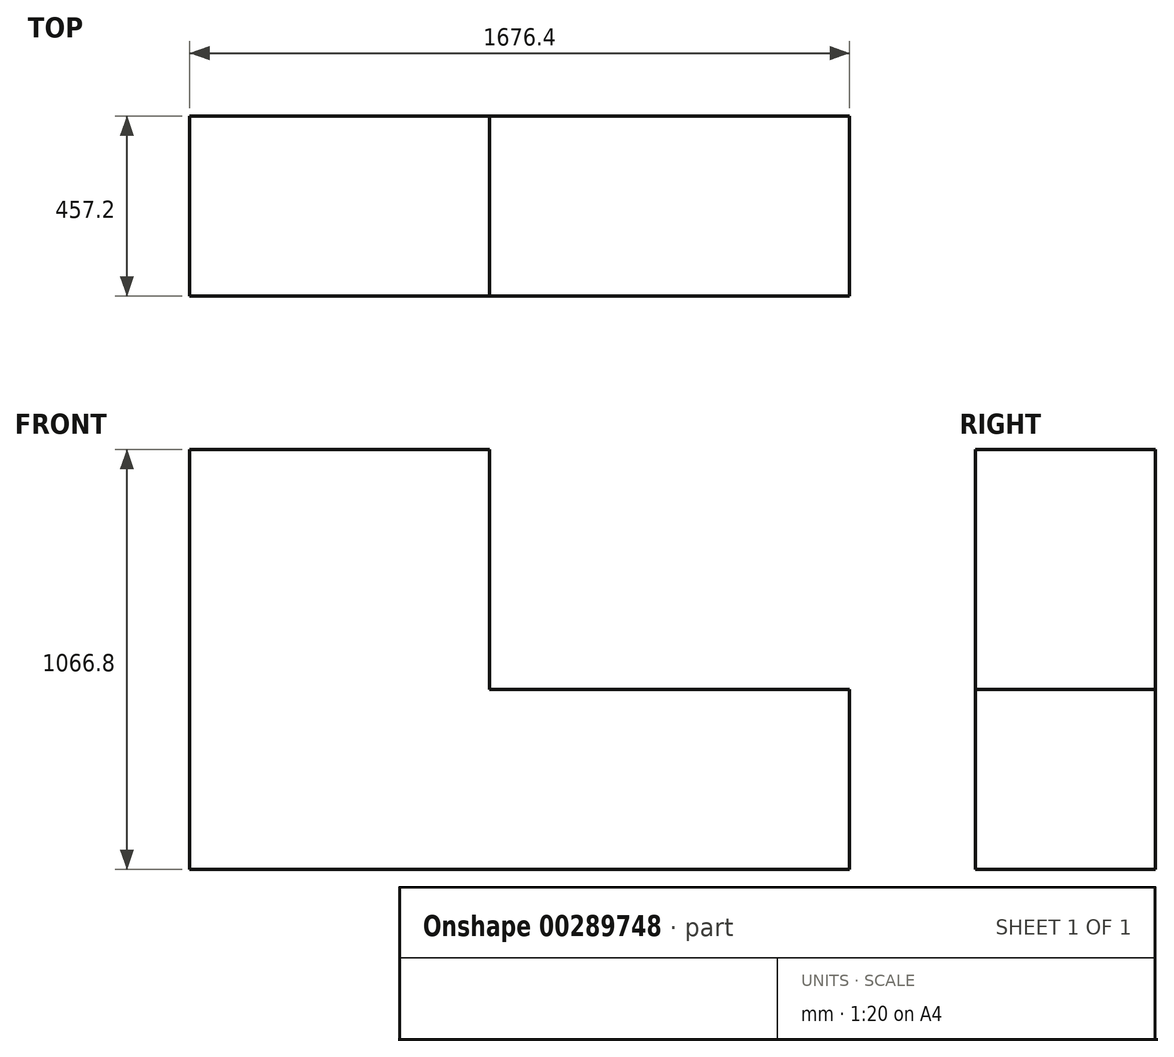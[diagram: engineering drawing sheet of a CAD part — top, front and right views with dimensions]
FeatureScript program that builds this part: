
annotation { "Feature Type Name" : "Feature", "Feature Type Description" : "" }
export const myFeature = defineFeature(function(context is Context, id is Id, definition is map)
    precondition{}
    {
        {
            var Q0;
            Q0=qCreatedBy(makeId("Front.planeOp"),FACE);
            var sketch = newSketch(context, id + "F0", { "sketchPlane" : qUnion([Q0])});
            skLineSegment(sketch, "E0.bottom", {"start": v(838.2, -533.4) * mm, "end": v(-838.2, -533.4) * mm});
            skLineSegment(sketch, "E0.top", {"start": v(838.2, 533.4) * mm, "end": v(-838.2, 533.4) * mm});
            skLineSegment(sketch, "E0.left", {"start": v(838.2, -533.4) * mm, "end": v(838.2, 533.4) * mm});
            skLineSegment(sketch, "E0.right", {"start": v(-838.2, -533.4) * mm, "end": v(-838.2, 533.4) * mm});
            skPoint(sketch, "E0.middle", {"position": v(0, 0) * mm});
            skLineSegment(sketch, "E1.bottom", {"start": v(838.2, 533.4) * mm, "end": v(-76.2, 533.4) * mm});
            skLineSegment(sketch, "E1.top", {"start": v(838.2, -76.2) * mm, "end": v(-76.2, -76.2) * mm});
            skLineSegment(sketch, "E1.left", {"start": v(838.2, 533.4) * mm, "end": v(838.2, -76.2) * mm});
            skLineSegment(sketch, "E1.right", {"start": v(-76.2, 533.4) * mm, "end": v(-76.2, -76.2) * mm});
            skSolve(sketch);
        }
        {
            var Q0;
            {var subQ1=sQuery(id+"F0.wireOp",EDGE,"E0.bottom");Q0=makeQuery(id+"F0.imprint","IMPRINT",FACE,{"disambiguationData":[TD([[makeQuery(id+"F0.imprint","IMPRINT",EDGE,{"derivedFrom":subQ1}),-1.0]])]});}
            extrude(context, id + "F1", {"entities" : qUnion([Q0]), "depth" : 457.2 * mm, "offsetDistance" : 30.48 * mm});
        }
    });
